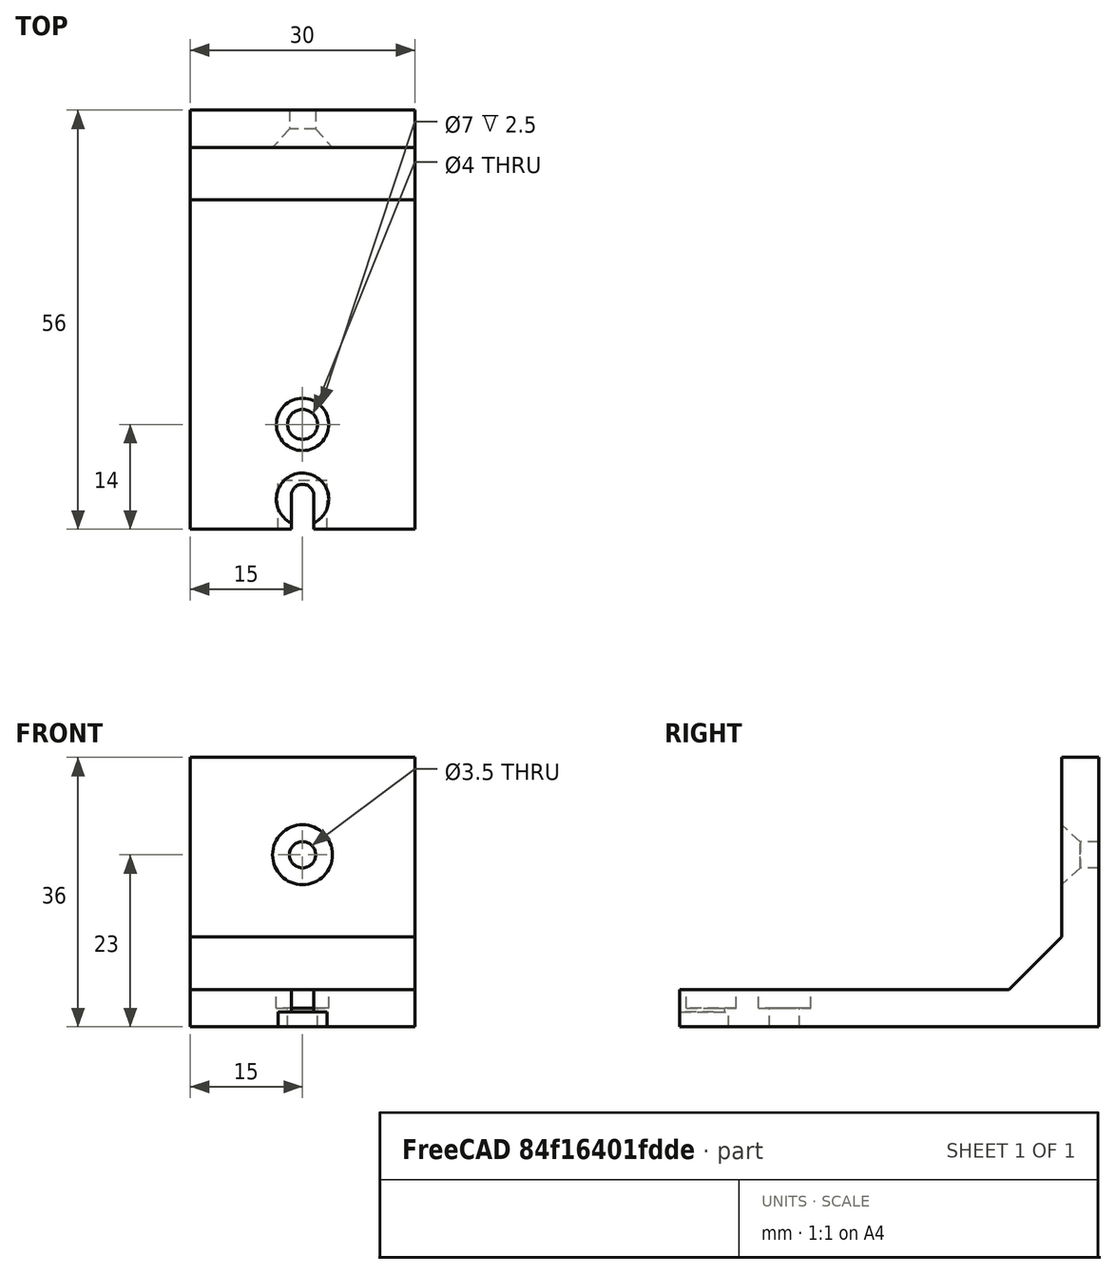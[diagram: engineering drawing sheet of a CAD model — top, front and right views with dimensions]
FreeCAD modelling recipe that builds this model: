
FCSTD DOCUMENT  (FreeCAD 0.19R24267 +99 (Git))
Label: porta_rab_sheka
License: Creative Commons Attribution-ShareAlike
LicenseURL: http://creativecommons.org/licenses/by-sa/4.0/
objects: Part::Cut×6, Part::Cylinder×5, Part::Box×4, Part::MultiFuse×2, Part::Cone×1, Part::Fuse×1, Part::Chamfer×1, Mesh::Feature×1
note: 20 computed .brp shape members not serialized (recipe doc carries the construction recipe); baked Part::Feature solids carry a one-line shape summary decoded from their .brp

FEATURE [Part::Box] Box  label="Cube"
  AttacherType = Attacher::AttachEngine3D
  Height = 5
  Length = 30
  Width = 56
FEATURE [Part::Box] Box001  label="Cube001"
  AttacherType = Attacher::AttachEngine3D
  Height = 36
  Length = 30
  Placement = pos=(0,51,0) rot=(0,0,1;0rad)
  Width = 5
FEATURE [Part::MultiFuse] Fusion  label="la_ele"
  Refine = true
  Shapes = -> [Box,Box001]
FEATURE [Part::Cylinder] Cylinder
  Angle = 360
  AttacherType = Attacher::AttachEngine3D
  Height = 10
  Radius = 1.5
FEATURE [Part::Box] Box002  label="Cube002"
  AttacherType = Attacher::AttachEngine3D
  Height = 10
  Length = 3
  Placement = pos=(-1.5,-10,0) rot=(0,0,1;0rad)
  Width = 10
FEATURE [Part::MultiFuse] Fusion001
  Placement = pos=(15,4.5,0) rot=(0,0,1;0rad)
  Refine = true
  Shapes = -> [Box002,Cylinder]
FEATURE [Part::Cylinder] Cylinder001
  Angle = 360
  AttacherType = Attacher::AttachEngine3D
  Height = 10
  Placement = pos=(15,14,0) rot=(0,0,1;0rad)
  Radius = 2
FEATURE [Part::Box] Box003  label="Cube003"
  AttacherType = Attacher::AttachEngine3D
  Height = 10
  Length = 6.5
  Placement = pos=(11.75,0,-8) rot=(0,0,1;0rad)
  Width = 6.5
FEATURE [Part::Cylinder] Cylinder002
  Angle = 360
  AttacherType = Attacher::AttachEngine3D
  Height = 10
  Placement = pos=(15,4,2.5) rot=(0,0,1;0rad)
  Radius = 3.5
FEATURE [Part::Cylinder] Cylinder003
  Angle = 360
  AttacherType = Attacher::AttachEngine3D
  Height = 10
  Placement = pos=(15,14,2.5) rot=(0,0,1;0rad)
  Radius = 3.5
FEATURE [Part::Cone] Cone
  Angle = 360
  AttacherType = Attacher::AttachEngine3D
  Height = 2.5
  Radius1 = 1.75
  Radius2 = 4
FEATURE [Part::Cylinder] Cylinder004
  Angle = 360
  AttacherType = Attacher::AttachEngine3D
  Height = 10
  Placement = pos=(0,0,-8) rot=(0,0,1;0rad)
  Radius = 1.75
FEATURE [Part::Fuse] Fusion002  label="agujero_tornillo_madera"
  Base = -> Cone
  Placement = pos=(15,53.5,23) rot=(1,0,0;1.5708rad)
  Refine = true
  Tool = -> Cylinder004
FEATURE [Part::Chamfer] Chamfer
  Base = -> Fusion
  Edges = 1 edges r=7: [Edge2]
FEATURE [Part::Cut] Cut
  Base = -> Chamfer
  Tool = -> Cylinder003
FEATURE [Part::Cut] Cut001
  Base = -> Cut
  Tool = -> Cylinder001
FEATURE [Part::Cut] Cut002
  Base = -> Cut001
  Tool = -> Cylinder002
FEATURE [Part::Cut] Cut003
  Base = -> Cut002
  Tool = -> Fusion001
FEATURE [Part::Cut] Cut004
  Base = -> Cut003
  Tool = -> Box003
FEATURE [Part::Cut] Cut005
  Base = -> Cut004
  Tool = -> Fusion002
FEATURE [Mesh::Feature] Mesh  label="Cut005 (Meshed)"
